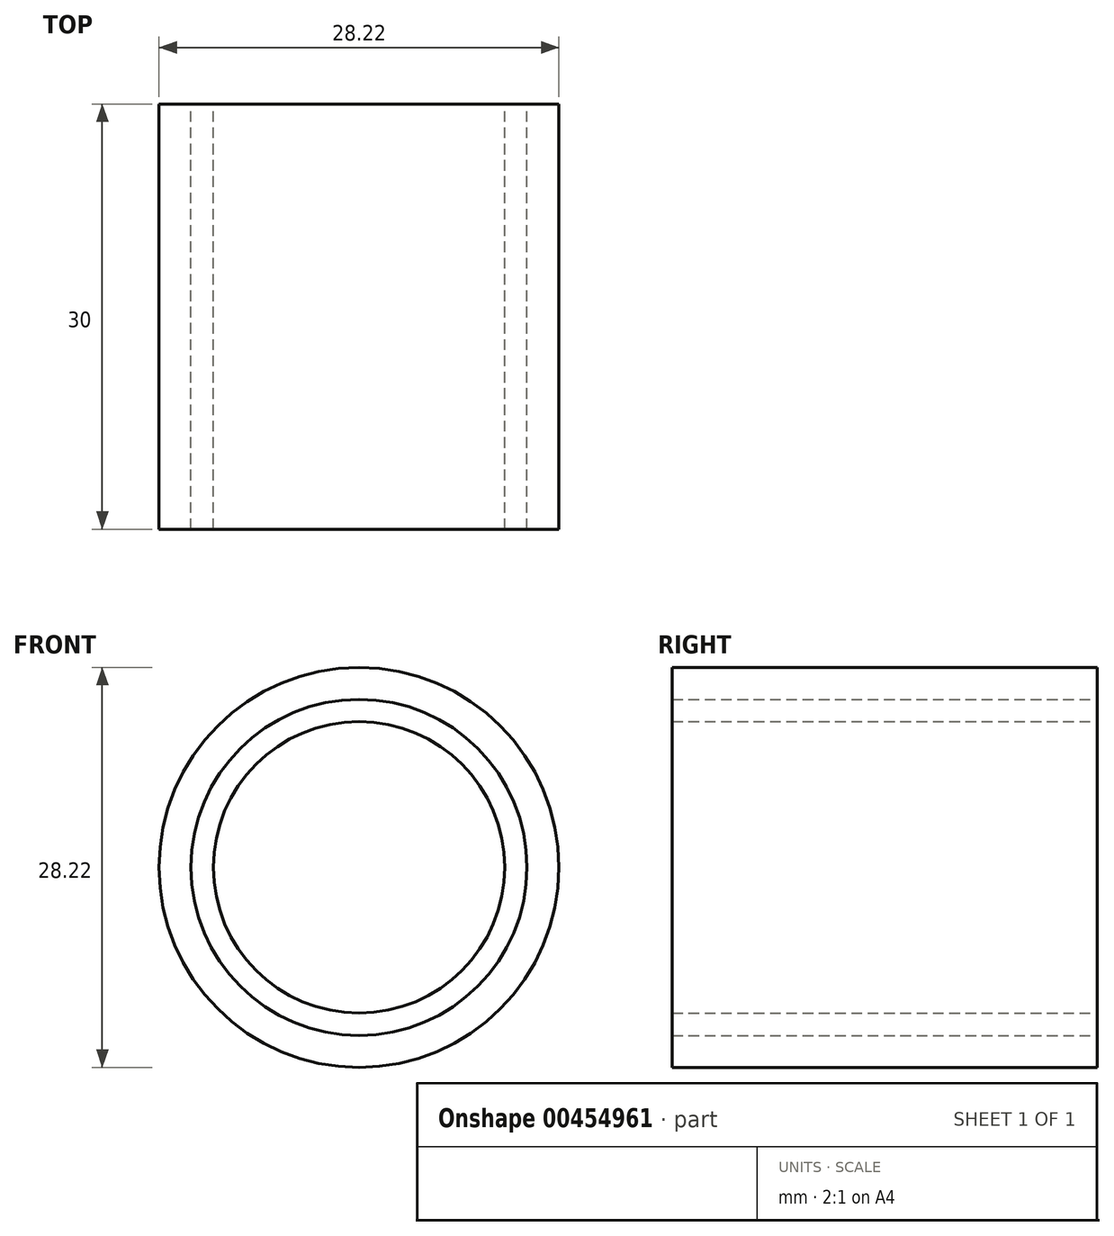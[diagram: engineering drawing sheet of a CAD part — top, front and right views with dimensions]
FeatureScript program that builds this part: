
annotation { "Feature Type Name" : "Feature", "Feature Type Description" : "" }
export const myFeature = defineFeature(function(context is Context, id is Id, definition is map)
    precondition{}
    {
        {
            var Q0;
            Q0=qCreatedBy(makeId("Front.planeOp"),FACE);
            var sketch = newSketch(context, id + "F0", { "sketchPlane" : qUnion([Q0])});
            skCircle(sketch, "E0", {"center": v(0, 0) * mm, "radius": 10.28 * mm});
            skSolve(sketch);
        }
        {
            var Q0;
            Q0 = qSketchRegion(id + "F0", true);
            extrude(context, id + "F1", {"entities" : qUnion([Q0]), "depth" : 30 * mm});
        }
        {
            var Q0;
            Q0=qCreatedBy(makeId("Front.planeOp"),FACE);
            var sketch = newSketch(context, id + "F2", { "sketchPlane" : qUnion([Q0])});
            skCircle(sketch, "E1", {"center": v(0, 0) * mm, "radius": 11.86 * mm});
            skCircle(sketch, "E2", {"center": v(0, 0) * mm, "radius": 14.11 * mm});
            skSolve(sketch);
        }
        {
            var Q0;
            Q0 = qSketchRegion(id + "F2", true);
            extrude(context, id + "F3", {"entities" : qUnion([Q0]), "depth" : 30 * mm});
        }
    });
